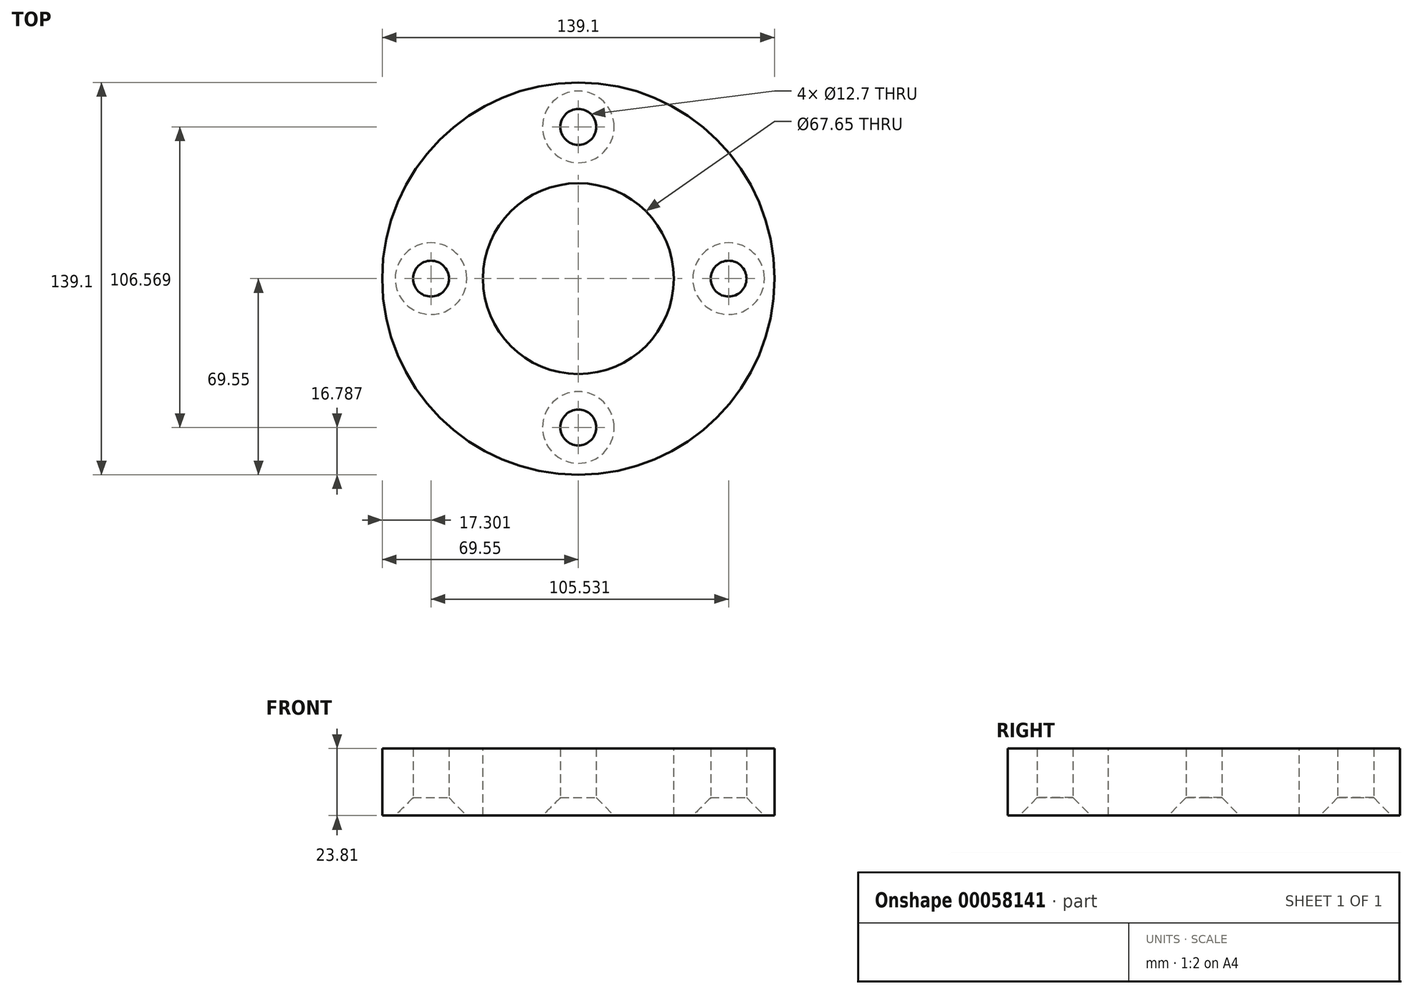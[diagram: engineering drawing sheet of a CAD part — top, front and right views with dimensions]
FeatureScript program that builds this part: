
annotation { "Feature Type Name" : "Feature", "Feature Type Description" : "" }
export const myFeature = defineFeature(function(context is Context, id is Id, definition is map)
    precondition{}
    {
        {
            var Q0;
            Q0=qCreatedBy(makeId("Front.planeOp"),FACE);
            var sketch = newSketch(context, id + "F0", { "sketchPlane" : qUnion([Q0])});
            skLineSegment(sketch, "E0.bottom", {"start": v(-69.55, 23.81) * mm, "end": v(-33.83, 23.81) * mm});
            skLineSegment(sketch, "E0.top", {"start": v(-69.55, 0) * mm, "end": v(-33.83, 0) * mm});
            skLineSegment(sketch, "E0.left", {"start": v(-69.55, 23.81) * mm, "end": v(-69.55, 0) * mm});
            skLineSegment(sketch, "E0.right", {"start": v(-33.83, 23.81) * mm, "end": v(-33.83, 0) * mm});
            skLineSegment(sketch, "E1", {"start": v(-33.83, 0) * mm, "end": v(0, 0) * mm});
            skLineSegment(sketch, "E2", {"start": v(0, 48.7) * mm, "end": v(0, -57.91) * mm});
            skSolve(sketch);
        }
        {
            var Q0;
            Q0=makeQuery(id+"F0.imprint","IMPRINT",FACE,{"disambiguationData":[TD([[makeQuery(id+"F0.imprint","IMPRINT",EDGE,{"derivedFrom":sQuery(id+"F0.wireOp",EDGE,"E0.bottom")}),-1.0]])]});
            var Q1;
            Q1=sQuery(id+"F0.wireOp",EDGE,"E2");
            revolve(context, id + "F1", {"entities" : qUnion([Q0]), "axis" : qUnion([Q1]), "revolveType" : RevolveType.FULL});
        }
        {
            var Q0;
            Q0=qCreatedBy(makeId("Top.planeOp"),FACE);
            var sketch = newSketch(context, id + "F2", { "sketchPlane" : qUnion([Q0])});
            skLineSegment(sketch, "E3", {"start": v(0, 53.8) * mm, "end": v(53.28, 0) * mm});
            skLineSegment(sketch, "E4", {"start": v(53.28, 0) * mm, "end": v(0, -52.76) * mm});
            skLineSegment(sketch, "E5", {"start": v(0, -52.76) * mm, "end": v(-52.25, 0) * mm});
            skLineSegment(sketch, "E6", {"start": v(-52.25, 0) * mm, "end": v(0, 53.8) * mm});
            skSolve(sketch);
        }
        {
            var Q0;
            Q0=sQuery(id+"F2.wireOp",VERTEX,"E4.start");
            var Q1;
            Q1=sQuery(id+"F2.wireOp",VERTEX,"E5.start");
            var Q2;
            Q2=sQuery(id+"F2.wireOp",VERTEX,"E6.start");
            var Q3;
            Q3=sQuery(id+"F2.wireOp",VERTEX,"E3.start");
            var Q4;
            Q4=makeQuery(id+"F1.opRevolve","SWEPT_BODY",BODY,{"disambiguationData":[OSD([sQuery(id+"F0.wireOp",EDGE,"E0.bottom"),sQuery(id+"F0.wireOp",EDGE,"E0.top"),sQuery(id+"F0.wireOp",EDGE,"E0.left"),sQuery(id+"F0.wireOp",EDGE,"E0.right")])]});
            hole(context, id + "F3", {"style" : HoleStyle.C_SINK, "holeDiameter" : 12.7 * mm, "cSinkDiameter" : 25.4 * mm, "endStyle" : HoleEndStyle.THROUGH, "oppositeDirection" : true, "locations" : qUnion([Q0, Q1, Q2, Q3]), "scope" : qUnion([Q4]), "cSinkAngle" : 90 * degree});
        }
    });
